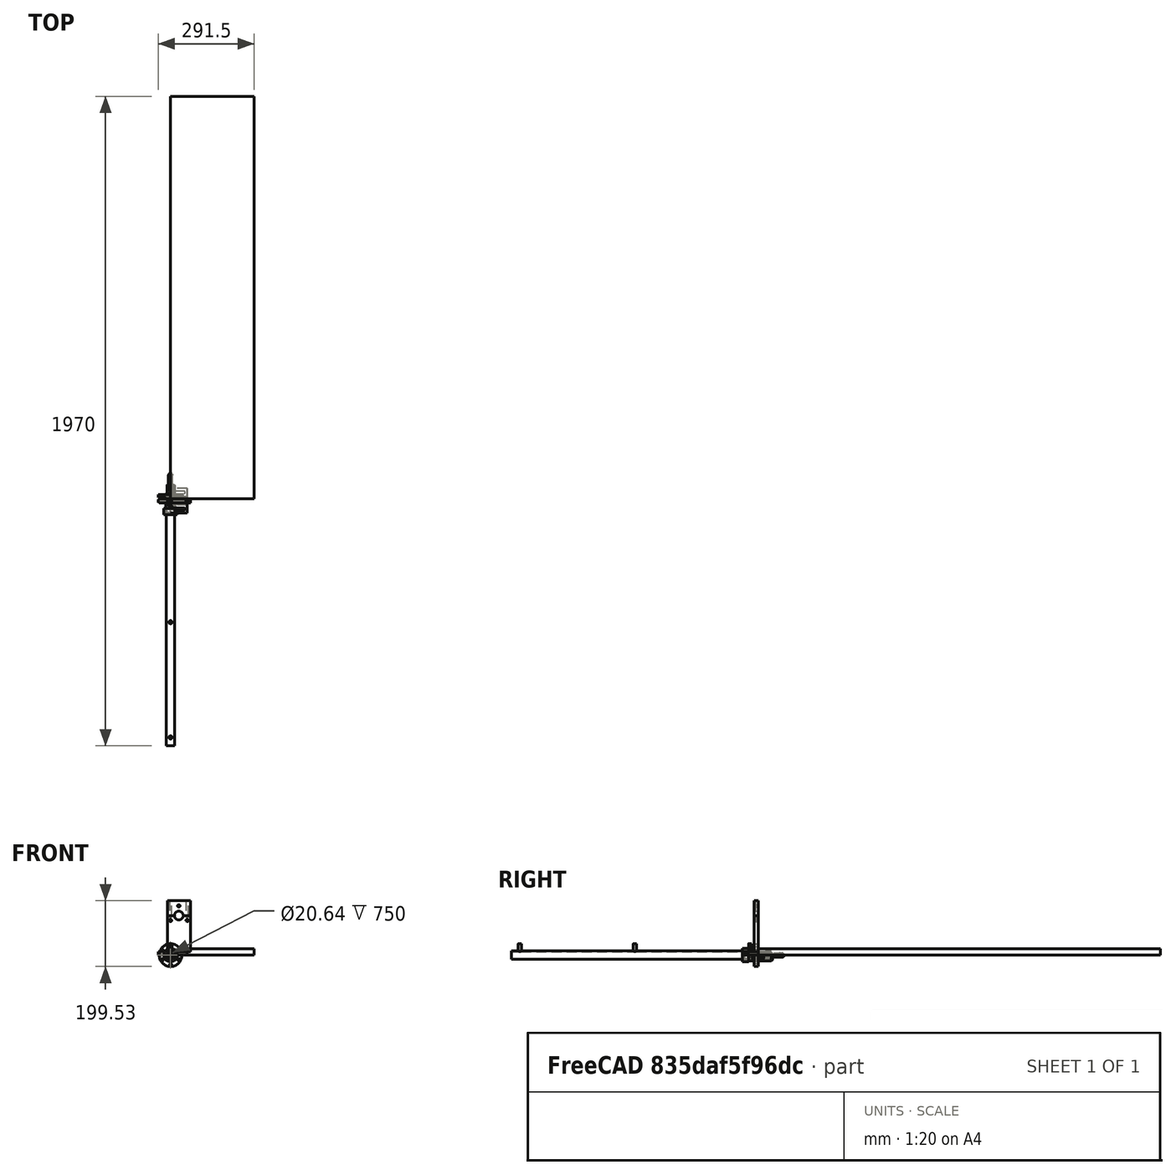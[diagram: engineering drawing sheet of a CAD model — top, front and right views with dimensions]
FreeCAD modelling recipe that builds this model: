
FCSTD DOCUMENT  (FreeCAD 0.19R24291 (Git))
Label: CEAS2
License: All rights reserved
LicenseURL: http://en.wikipedia.org/wiki/All_rights_reserved
objects: Part::Feature×57, Sketcher::SketchObject×41, PartDesign::Pad×41, PartDesign::Body×41, Part::Cut×34, Part::Compound2×12, App::Part×10, TechDraw::DrawViewPart×8, TechDraw::DrawViewDimension×4, TechDraw::DrawViewBalloon×4, TechDraw::DrawViewAnnotation×4, Part::MultiFuse×3, TechDraw::DrawSVGTemplate×1, TechDraw::DrawPage×1
note: 258 computed .brp shape members not serialized (recipe doc carries the construction recipe); baked Part::Feature solids carry a one-line shape summary decoded from their .brp

FEATURE [Sketcher::SketchObject] Sketch
  FullyConstrained = true
  MapMode = 5
  Support = -> [XY_Plane001]
  sketch-geometry (4):
    g0: LineSegment StartX=0 StartY=1220 StartZ=0 EndX=254 EndY=1220 EndZ=0
    g1: LineSegment StartX=254 StartY=1220 StartZ=0 EndX=254 EndY=0 EndZ=0
    g2: LineSegment StartX=254 StartY=0 StartZ=0 EndX=0 EndY=0 EndZ=0
    g3: LineSegment StartX=0 StartY=0 StartZ=0 EndX=0 EndY=1220 EndZ=0
  constraints (11):
    c: Coincident(g0,g1)
    c: Coincident(g1,g2)
    c: Coincident(g2,g3)
    c: Coincident(g3,g0)
    c: Horizontal(g0)
    c: Horizontal(g2)
    c: Vertical(g1)
    c: Vertical(g3)
    c: DistanceY(g3,g3) = 1220
    c: Coincident(g2,g-1)
    c: DistanceX(g2,g2) = 254
FEATURE [PartDesign::Pad] Pad
  AllowMultiFace = false
  Direction = (1,1,1)
  Length = 19.05
  Length2 = 100
  Profile = -> Sketch
  Type = 0
FEATURE [PartDesign::Body] Body  label="BasePlate001"
  Group = -> [Sketch,Pad]
  Origin = -> Origin001
  Tip = -> Pad
FEATURE [App::Part] Part  label="BasePlate"
  Group = -> [Body]
  Origin = -> Origin
FEATURE [Sketcher::SketchObject] Sketch001
  FullyConstrained = true
  MapMode = 5
  Placement = pos=(0,0,0) rot=(1,0,0;1.5708rad)
  Support = -> [XZ_Plane003]
  sketch-geometry (6):
    g0: LineSegment StartX=0 StartY=0 StartZ=0 EndX=0 EndY=110 EndZ=0
    g1: LineSegment StartX=0 StartY=110 StartZ=0 EndX=21.675 EndY=110 EndZ=0
    g2: ArcOfCircle CenterX=35 CenterY=110 CenterZ=0 NormalX=0 NormalY=0 NormalZ=1 AngleXU=0 Radius=13.325 StartAngle=3.14159 EndAngle=6.28319
    g3: LineSegment StartX=48.325 StartY=110 StartZ=0 EndX=70 EndY=110 EndZ=0
    g4: LineSegment StartX=70 StartY=110 StartZ=0 EndX=70 EndY=0 EndZ=0
    g5: LineSegment StartX=70 StartY=0 StartZ=0 EndX=0 EndY=0 EndZ=0
  constraints (18):
    c: DistanceX(g5,g5) = 70
    c: Coincident(g5,g0)
    c: Coincident(g1,g2)
    c: Coincident(g1,g0)
    c: Coincident(g2,g3)
    c: Coincident(g3,g4)
    c: Coincident(g5,g4)
    c: Diameter(g2) = 26.65
    c: Parallel(g0,g4)
    c: DistanceY(g4,g4) = 110
    c: Equal(g0,g4)
    c: Equal(g3,g1)
    c: Perpendicular(g5,g0)
    c: Perpendicular(g4,g3)
    c: Vertical(g0)
    c: Perpendicular(g0,g1)
    c: Coincident(g0,g-1)
    c: DistanceX(g1,g2) = 26.65
FEATURE [Sketcher::SketchObject] Sketch002
  FullyConstrained = true
  MapMode = 5
  Placement = pos=(0,0,0) rot=(1,0,0;1.5708rad)
  Support = -> [XZ_Plane004]
  sketch-geometry (6):
    g0: LineSegment StartX=-20 StartY=110 StartZ=0 EndX=-20 EndY=155 EndZ=0
    g1: LineSegment StartX=-20 StartY=155 StartZ=0 EndX=50 EndY=155 EndZ=0
    g2: LineSegment StartX=50 StartY=155 StartZ=0 EndX=50 EndY=110 EndZ=0
    g3: LineSegment StartX=50 StartY=110 StartZ=0 EndX=28.325 EndY=110 EndZ=0
    g4: LineSegment StartX=-20 StartY=110 StartZ=0 EndX=1.675 EndY=110 EndZ=0
    g5: ArcOfCircle CenterX=15 CenterY=110 CenterZ=0 NormalX=0 NormalY=0 NormalZ=1 AngleXU=0 Radius=13.325 StartAngle=2.48459e-06 EndAngle=3.14159
  constraints (19):
    c: Diameter(g5) = 26.65
    c: DistanceX(g1,g1) = 70
    c: Coincident(g0,g1)
    c: Coincident(g1,g2)
    c: Coincident(g2,g3)
    c: Coincident(g5,g3)
    c: Coincident(g5,g4)
    c: Coincident(g0,g4)
    c: DistanceY(g2,g2) = 45
    c: Equal(g2,g0)
    c: Horizontal(g4)
    c: Equal(g4,g3)
    c: Vertical(g0)
    c: Horizontal(g1)
    c: Perpendicular(g2,g1)
    c: Perpendicular(g2,g3)
    c: DistanceY(g-1,g0) = 110
    c: DistanceX(g-1,g2) = 50
    c: DistanceX(g4,g3) = 26.65
FEATURE [PartDesign::Pad] Pad001
  AllowMultiFace = false
  Direction = (1,1,1)
  Length = 12.7
  Length2 = 100
  Placement = pos=(0,0,0) rot=(1,0,0;1.5708rad)
  Profile = -> Sketch001
  Type = 0
FEATURE [PartDesign::Body] Body001  label="BraceLower"
  Group = -> [Sketch001,Pad001]
  Origin = -> Origin003
  Placement = pos=(-10,0,10) rot=(0,0,1;0rad)
  Tip = -> Pad001
FEATURE [PartDesign::Pad] Pad002
  AllowMultiFace = false
  Direction = (1,1,1)
  Length = 12.7
  Length2 = 100
  Placement = pos=(0,0,0) rot=(1,0,0;1.5708rad)
  Profile = -> Sketch002
  Type = 0
FEATURE [PartDesign::Body] Body002  label="Brace1Upper"
  Group = -> [Sketch002,Pad002]
  Origin = -> Origin004
  Placement = pos=(10,0,10) rot=(0,0,1;0rad)
  Tip = -> Pad002
FEATURE [Part::Feature] Solid  label="19227-E0W"
  Placement = pos=(25,-6.35,5.1905) rot=(1,0,0;1.5708rad)
  shape: bbox 50 x 75 x 10 mm, 234 faces (baked)
FEATURE [Part::Feature] Solid002  label="19225-E0W"
  Placement = pos=(0,0,5) rot=(1,0,0;1.5708rad)
  shape: bbox 75 x 24.99 x 10 mm, 221 faces (baked)
FEATURE [Part::Feature] Solid003
  shape: bbox 25 x 75 x 25 mm, 25 faces (baked)
FEATURE [Part::Feature] Solid004
  shape: bbox 15.88 x 5.969 x 15.88 mm, 19 faces (baked)
FEATURE [Part::Feature] Solid005
  shape: bbox 14.48 x 14.48 x 16.13 mm, 310 faces (baked)
FEATURE [Part::Feature] Solid006
  shape: bbox 2.997 x 2.997 x 3.556 mm, 8 faces (baked)
FEATURE [Part::Feature] Solid007
  shape: bbox 3.52 x 3.049 x 7.519 mm, 25 faces (baked)
FEATURE [Part::Feature] Solid008
  shape: bbox 3.482 x 3.482 x 3.175 mm, 21 faces (baked)
FEATURE [Part::Compound2] Compound  label="23133-E0W"
  Links = -> [Solid003,Solid004,Solid005,Solid006,Solid007,Solid008]
  Placement = pos=(-1.27,-4.75,41.95) rot=(1,0,0;1.5708rad)
FEATURE [Part::Feature] Solid009
  shape: bbox 12.67 x 75.01 x 12.67 mm, 32 faces (baked)
FEATURE [Part::Feature] Solid010
  shape: bbox 4.001 x 12 x 4.001 mm, 40 faces (baked)
FEATURE [Part::Compound2] Compound001  label="0332-E0W"
  Links = -> [Solid009,Solid010]
  Placement = pos=(0,0,22.896) rot=(1,0,0;1.5708rad)
FEATURE [Part::Feature] Solid011
  shape: bbox 30.48 x 37.34 x 10.16 mm, 236 faces (baked)
FEATURE [Part::Feature] Solid012
  shape: bbox 26.29 x 26.29 x 2.032 mm, 29 faces (baked)
FEATURE [Part::Compound2] Compound002  label="0001-E0W"
  Links = -> [Solid011,Solid012]
  Placement = pos=(0,-5.05,120) rot=(1,0,0;1.5708rad)
FEATURE [App::Part] Part003  label="Lens1"
  Group = -> [Solid002,Solid008,Solid006,Solid003,Solid005,Solid007,Solid004,Compound,Solid009,Solid010,Compound001,Solid012,Solid011,Compound002]
  Origin = -> Origin008
  Placement = pos=(127,100,19.05) rot=(0,0,1;0rad)
FEATURE [Part::Feature] Solid013  label="19225-E0W001"
  Placement = pos=(0,0,5) rot=(1,0,0;1.5708rad)
  shape: bbox 75 x 24.99 x 10 mm, 221 faces (baked)
FEATURE [Part::Feature] Solid014
  shape: bbox 25 x 75 x 25 mm, 25 faces (baked)
FEATURE [Part::Feature] Solid015
  shape: bbox 15.88 x 5.969 x 15.88 mm, 19 faces (baked)
FEATURE [Part::Feature] Solid016
  shape: bbox 14.48 x 14.48 x 16.13 mm, 310 faces (baked)
FEATURE [Part::Feature] Solid017
  shape: bbox 2.997 x 2.997 x 3.556 mm, 8 faces (baked)
FEATURE [Part::Feature] Solid018
  shape: bbox 3.52 x 3.049 x 7.519 mm, 25 faces (baked)
FEATURE [Part::Feature] Solid019
  shape: bbox 3.482 x 3.482 x 3.175 mm, 21 faces (baked)
FEATURE [Part::Compound2] Compound003  label="23133-E0W001"
  Links = -> [Solid014,Solid015,Solid016,Solid017,Solid018,Solid019]
  Placement = pos=(-1.27,-4.75,41.95) rot=(1,0,0;1.5708rad)
FEATURE [Part::Feature] Solid020
  shape: bbox 12.67 x 75.01 x 12.67 mm, 32 faces (baked)
FEATURE [Part::Feature] Solid021
  shape: bbox 4.001 x 12 x 4.001 mm, 40 faces (baked)
FEATURE [Part::Compound2] Compound004  label="0332-E0W001"
  Links = -> [Solid020,Solid021]
  Placement = pos=(0,0,22.896) rot=(1,0,0;1.5708rad)
FEATURE [Part::Feature] Solid022
  shape: bbox 30.48 x 37.34 x 10.16 mm, 236 faces (baked)
FEATURE [Part::Feature] Solid023
  shape: bbox 26.29 x 26.29 x 2.032 mm, 29 faces (baked)
FEATURE [Part::Compound2] Compound005  label="0001-E0W001"
  Links = -> [Solid022,Solid023]
  Placement = pos=(0,-5.05,120) rot=(1,0,0;1.5708rad)
FEATURE [App::Part] Part004  label="Lens2"
  Group = -> [Solid013,Solid019,Solid017,Solid014,Solid016,Solid018,Solid015,Compound003,Solid020,Solid021,Compound004,Solid023,Solid022,Compound005]
  Origin = -> Origin009
  Placement = pos=(127,200,19.05) rot=(0,0,1;0rad)
FEATURE [Part::Feature] Solid024
  shape: bbox 26.29 x 26.29 x 2.032 mm, 29 faces (baked)
FEATURE [Part::Feature] Solid025
  shape: bbox 30.48 x 37.34 x 10.16 mm, 236 faces (baked)
FEATURE [Part::Compound2] Compound006  label="0001-E0W002"
  Links = -> [Solid025,Solid024]
  Placement = pos=(0,-5.05,120) rot=(1,0,0;1.5708rad)
FEATURE [Part::Feature] Solid026
  shape: bbox 2.997 x 2.997 x 3.556 mm, 8 faces (baked)
FEATURE [Part::Feature] Solid027
  shape: bbox 14.48 x 14.48 x 16.13 mm, 310 faces (baked)
FEATURE [Part::Feature] Solid028
  shape: bbox 25 x 75 x 25 mm, 25 faces (baked)
FEATURE [Part::Feature] Solid029
  shape: bbox 15.88 x 5.969 x 15.88 mm, 19 faces (baked)
FEATURE [Part::Feature] Solid030
  shape: bbox 3.482 x 3.482 x 3.175 mm, 21 faces (baked)
FEATURE [Part::Feature] Solid031
  shape: bbox 3.52 x 3.049 x 7.519 mm, 25 faces (baked)
FEATURE [Part::Compound2] Compound007  label="23133-E0W002"
  Links = -> [Solid028,Solid029,Solid027,Solid026,Solid031,Solid030]
  Placement = pos=(-1.27,-4.75,41.95) rot=(1,0,0;1.5708rad)
FEATURE [Part::Feature] Solid032  label="19225-E0W002"
  Placement = pos=(0,0,5) rot=(1,0,0;1.5708rad)
  shape: bbox 75 x 24.99 x 10 mm, 221 faces (baked)
FEATURE [Part::Feature] Solid033
  shape: bbox 12.67 x 75.01 x 12.67 mm, 32 faces (baked)
FEATURE [Part::Feature] Solid034
  shape: bbox 4.001 x 12 x 4.001 mm, 40 faces (baked)
FEATURE [Part::Compound2] Compound008  label="0332-E0W002"
  Links = -> [Solid033,Solid034]
  Placement = pos=(0,0,22.896) rot=(1,0,0;1.5708rad)
FEATURE [App::Part] Part005  label="Lens3"
  Group = -> [Solid032,Solid030,Solid026,Solid028,Solid027,Solid031,Solid029,Compound007,Solid033,Solid034,Compound008,Solid024,Solid025,Compound006]
  Origin = -> Origin010
  Placement = pos=(127,1150,19.05) rot=(0,0,1;0rad)
FEATURE [Sketcher::SketchObject] Sketch005
  FullyConstrained = true
  MapMode = 5
  Placement = pos=(0,0,0) rot=(1,0,0;1.5708rad)
  Support = -> [XZ_Plane015]
  sketch-geometry (2):
    g0: Circle CenterX=0 CenterY=0 CenterZ=0 NormalX=0 NormalY=0 NormalZ=1 AngleXU=0 Radius=12.7
    g1: Circle CenterX=0 CenterY=0 CenterZ=0 NormalX=0 NormalY=0 NormalZ=1 AngleXU=0 Radius=10.3187
  constraints (4):
    c: Coincident(g0,g-1)
    c: Coincident(g1,g0)
    c: Diameter(g0) = 25.4
    c: Diameter(g1) = 20.6375
FEATURE [PartDesign::Pad] Pad005
  Direction = (1,1,1)
  Length = 750
  Length2 = 100
  Placement = pos=(0,0,0) rot=(1,0,0;1.5708rad)
  Profile = -> Sketch005
  Type = 0
FEATURE [PartDesign::Body] Body005
  Group = -> [Sketch005,Pad005]
  Origin = -> Origin015
  Tip = -> Pad005
FEATURE [Sketcher::SketchObject] Sketch006
  FullyConstrained = true
  MapMode = 5
  Support = -> [XY_Plane016]
  sketch-geometry (2):
    g0: Circle CenterX=0 CenterY=0 CenterZ=0 NormalX=0 NormalY=0 NormalZ=1 AngleXU=0 Radius=4.7625
    g1: Circle CenterX=0 CenterY=0 CenterZ=0 NormalX=0 NormalY=0 NormalZ=1 AngleXU=0 Radius=3.8695
  constraints (4):
    c: Coincident(g0,g-1)
    c: Coincident(g1,g0)
    c: Diameter(g0) = 9.525
    c: Diameter(g1) = 7.739
FEATURE [PartDesign::Pad] Pad006
  Direction = (1,1,1)
  Length = 25.4
  Length2 = 100
  Profile = -> Sketch006
  Type = 0
FEATURE [PartDesign::Body] Body006
  Group = -> [Sketch006,Pad006]
  Origin = -> Origin016
  Placement = pos=(0,-25.4,9.55) rot=(0,0,1;0rad)
  Tip = -> Pad006
FEATURE [Sketcher::SketchObject] Sketch007
  FullyConstrained = true
  MapMode = 5
  Support = -> [XY_Plane017]
  sketch-geometry (2):
    g0: Circle CenterX=0 CenterY=0 CenterZ=0 NormalX=0 NormalY=0 NormalZ=1 AngleXU=0 Radius=4.7625
    g1: Circle CenterX=0 CenterY=0 CenterZ=0 NormalX=0 NormalY=0 NormalZ=1 AngleXU=0 Radius=3.8695
  constraints (4):
    c: Coincident(g0,g-1)
    c: Coincident(g1,g0)
    c: Diameter(g0) = 9.525
    c: Diameter(g1) = 7.739
FEATURE [PartDesign::Pad] Pad007
  Direction = (1,1,1)
  Length = 25.4
  Length2 = 100
  Profile = -> Sketch007
  Type = 0
FEATURE [PartDesign::Body] Body007
  Group = -> [Sketch007,Pad007]
  Origin = -> Origin017
  Placement = pos=(0,-375,9.55) rot=(0,0,1;0rad)
  Tip = -> Pad007
FEATURE [Sketcher::SketchObject] Sketch008
  FullyConstrained = true
  MapMode = 5
  Support = -> [XY_Plane018]
  sketch-geometry (2):
    g0: Circle CenterX=0 CenterY=0 CenterZ=0 NormalX=0 NormalY=0 NormalZ=1 AngleXU=0 Radius=4.7625
    g1: Circle CenterX=0 CenterY=0 CenterZ=0 NormalX=0 NormalY=0 NormalZ=1 AngleXU=0 Radius=3.8695
  constraints (4):
    c: Coincident(g0,g-1)
    c: Coincident(g1,g0)
    c: Diameter(g0) = 9.525
    c: Diameter(g1) = 7.739
FEATURE [PartDesign::Pad] Pad008
  Direction = (1,1,1)
  Length = 25.4
  Length2 = 100
  Profile = -> Sketch008
  Type = 0
FEATURE [PartDesign::Body] Body008
  Group = -> [Sketch008,Pad008]
  Origin = -> Origin018
  Placement = pos=(0,-724.6,9.55) rot=(0,0,1;0rad)
  Tip = -> Pad008
FEATURE [Sketcher::SketchObject] Sketch009
  FullyConstrained = true
  MapMode = 5
  Support = -> [XY_Plane020]
  sketch-geometry (1):
    g0: Circle CenterX=0 CenterY=0 CenterZ=0 NormalX=0 NormalY=0 NormalZ=1 AngleXU=0 Radius=4.7625
  constraints (2):
    c: Coincident(g0,g-1)
    c: Diameter(g0) = 9.525
FEATURE [PartDesign::Pad] Pad009
  Direction = (1,1,1)
  Length = 25.4
  Length2 = 100
  Profile = -> Sketch009
  Type = 0
FEATURE [PartDesign::Body] Body009
  Group = -> [Sketch009,Pad009]
  Origin = -> Origin019
  Placement = pos=(0,-25.4,0) rot=(0,0,1;0rad)
  Tip = -> Pad009
FEATURE [Sketcher::SketchObject] Sketch010
  FullyConstrained = true
  MapMode = 5
  Support = -> [XY_Plane021]
  sketch-geometry (1):
    g0: Circle CenterX=0 CenterY=0 CenterZ=0 NormalX=0 NormalY=0 NormalZ=1 AngleXU=0 Radius=4.7625
  constraints (2):
    c: Coincident(g0,g-1)
    c: Diameter(g0) = 9.525
FEATURE [PartDesign::Pad] Pad010
  Direction = (1,1,1)
  Length = 25.4
  Length2 = 100
  Profile = -> Sketch010
  Type = 0
FEATURE [PartDesign::Body] Body010
  Group = -> [Sketch010,Pad010]
  Origin = -> Origin020
  Placement = pos=(0,-375,0) rot=(0,0,1;0rad)
  Tip = -> Pad010
FEATURE [Sketcher::SketchObject] Sketch011
  FullyConstrained = true
  MapMode = 5
  Support = -> [XY_Plane022]
  sketch-geometry (1):
    g0: Circle CenterX=0 CenterY=0 CenterZ=0 NormalX=0 NormalY=0 NormalZ=1 AngleXU=0 Radius=4.7625
  constraints (2):
    c: Coincident(g0,g-1)
    c: Diameter(g0) = 9.525
FEATURE [PartDesign::Pad] Pad011
  Direction = (1,1,1)
  Length = 25.4
  Length2 = 100
  Profile = -> Sketch011
  Type = 0
FEATURE [PartDesign::Body] Body011
  Group = -> [Sketch011,Pad011]
  Origin = -> Origin021
  Placement = pos=(0,-724.6,0) rot=(0,0,1;0rad)
  Tip = -> Pad011
FEATURE [Part::Cut] Cut
  Base = -> Body005
  Tool = -> Body009
FEATURE [Part::Cut] Cut001
  Base = -> Cut
  Tool = -> Body010
FEATURE [Part::Cut] Cut002
  Base = -> Cut001
  Tool = -> Body011
FEATURE [Sketcher::SketchObject] Sketch012
  FullyConstrained = true
  MapMode = 5
  Placement = pos=(0,0,0) rot=(1,0,0;1.5708rad)
  Support = -> [XZ_Plane022]
  sketch-geometry (1):
    g0: Circle CenterX=0 CenterY=0 CenterZ=0 NormalX=0 NormalY=0 NormalZ=1 AngleXU=0 Radius=10.3187
  constraints (2):
    c: Coincident(g0,g-1)
    c: Diameter(g0) = 20.6375
FEATURE [PartDesign::Pad] Pad012
  Direction = (1,1,1)
  Length = 750
  Length2 = 100
  Placement = pos=(0,0,0) rot=(1,0,0;1.5708rad)
  Profile = -> Sketch012
  Type = 0
FEATURE [PartDesign::Body] Body012
  Group = -> [Sketch012,Pad012]
  Origin = -> Origin022
  Tip = -> Pad012
FEATURE [Part::Cut] Cut003
  Base = -> Body006
  Tool = -> Body012
FEATURE [Part::Cut] Cut004
  Base = -> Body007
  Tool = -> Body012
FEATURE [Part::Cut] Cut005
  Base = -> Body008
  Tool = -> Body012
FEATURE [Part::MultiFuse] Fusion
  Shapes = -> [Cut002,Cut005,Cut004,Cut003]
FEATURE [App::Part] Part007  label="Cavity"
  Group = -> [Body005,Body006,Body007,Body008,Body009,Body010,Body011,Cut,Cut001,Cut002,Body012,Cut005,Cut004,Cut003,Fusion]
  Origin = -> Origin014
  Placement = pos=(127,310.4,139.05) rot=(0,0,1;3.14159rad)
FEATURE [Sketcher::SketchObject] Sketch013
  FullyConstrained = true
  MapMode = 5
  Placement = pos=(0,0,0) rot=(1,0,0;1.5708rad)
  Support = -> [XZ_Plane024]
  sketch-geometry (2):
    g0: Circle CenterX=0 CenterY=0 CenterZ=0 NormalX=0 NormalY=0 NormalZ=1 AngleXU=0 Radius=34.5281
    g1: Circle CenterX=0 CenterY=0 CenterZ=0 NormalX=0 NormalY=0 NormalZ=1 AngleXU=0 Radius=14.2875
  constraints (4):
    c: Coincident(g0,g-1)
    c: Coincident(g1,g0)
    c: Diameter(g1) = 28.575
    c: Diameter(g0) = 69.0563
FEATURE [PartDesign::Pad] Pad013
  Direction = (1,1,1)
  Length = 12.7
  Length2 = 100
  Placement = pos=(0,0,0) rot=(1,0,0;1.5708rad)
  Profile = -> Sketch013
  Type = 0
FEATURE [PartDesign::Body] Body013
  Group = -> [Sketch013,Pad013]
  Origin = -> Origin024
  Tip = -> Pad013
FEATURE [Sketcher::SketchObject] Sketch014
  FullyConstrained = true
  MapMode = 5
  Placement = pos=(0,0,0) rot=(1,0,0;1.5708rad)
  Support = -> [XZ_Plane025]
  sketch-geometry (1):
    g0: Circle CenterX=0 CenterY=29.3687 CenterZ=0 NormalX=0 NormalY=0 NormalZ=1 AngleXU=0 Radius=3.57187
  constraints (3):
    c: PointOnObject(g0,g-2)
    c: DistanceY(g-1,g0) = 29.3687
    c: Diameter(g0) = 7.14375
FEATURE [PartDesign::Pad] Pad014
  Direction = (1,1,1)
  Length = 13
  Length2 = 100
  Placement = pos=(0,0,0) rot=(1,0,0;1.5708rad)
  Profile = -> Sketch014
  Type = 0
FEATURE [PartDesign::Body] Body014
  Group = -> [Sketch014,Pad014]
  Origin = -> Origin025
  Tip = -> Pad014
FEATURE [Part::Cut] Cut006
  Base = -> Body013
  Placement = pos=(0,0,0) rot=(0,1,0;1.0472rad)
  Tool = -> Body014
FEATURE [Part::Cut] Cut007
  Base = -> Cut006
  Placement = pos=(0,0,0) rot=(0,1,0;1.0472rad)
  Tool = -> Body014
FEATURE [Part::Cut] Cut008
  Base = -> Cut007
  Placement = pos=(0,0,0) rot=(0,1,0;1.0472rad)
  Tool = -> Body014
FEATURE [Part::Cut] Cut009
  Base = -> Cut008
  Placement = pos=(0,0,0) rot=(0,1,0;1.0472rad)
  Tool = -> Body014
FEATURE [Part::Cut] Cut010
  Base = -> Cut009
  Placement = pos=(0,0,0) rot=(0,1,0;1.0472rad)
  Tool = -> Body014
FEATURE [Part::Cut] Cut011
  Base = -> Cut010
  Tool = -> Body014
FEATURE [Sketcher::SketchObject] Sketch015
  FullyConstrained = true
  MapMode = 5
  Placement = pos=(0,0,0) rot=(1,0,0;1.5708rad)
  Support = -> [XZ_Plane026]
  sketch-geometry (2):
    g0: Circle CenterX=0 CenterY=0 CenterZ=0 NormalX=0 NormalY=0 NormalZ=1 AngleXU=0 Radius=12.7
    g1: Circle CenterX=0 CenterY=0 CenterZ=0 NormalX=0 NormalY=0 NormalZ=1 AngleXU=0 Radius=14.2875
  constraints (4):
    c: Coincident(g0,g-1)
    c: Coincident(g1,g0)
    c: Diameter(g0) = 25.4
    c: Diameter(g1) = 28.575
FEATURE [PartDesign::Pad] Pad015
  Direction = (1,1,1)
  Length = 29.21
  Length2 = 100
  Placement = pos=(0,0,0) rot=(1,0,0;1.5708rad)
  Profile = -> Sketch015
  Type = 0
FEATURE [PartDesign::Body] Body015
  Group = -> [Sketch015,Pad015]
  Origin = -> Origin026
  Placement = pos=(0,-0.16,0) rot=(0,0,1;0rad)
  Tip = -> Pad015
FEATURE [Sketcher::SketchObject] Sketch016
  FullyConstrained = true
  MapMode = 5
  Placement = pos=(0,0,0) rot=(1,0,0;1.5708rad)
  Support = -> [XZ_Plane027]
  sketch-geometry (2):
    g0: Circle CenterX=0 CenterY=0 CenterZ=0 NormalX=0 NormalY=0 NormalZ=1 AngleXU=0 Radius=12.7
    g1: Circle CenterX=0 CenterY=0 CenterZ=0 NormalX=0 NormalY=0 NormalZ=1 AngleXU=0 Radius=16.6687
  constraints (4):
    c: Coincident(g0,g-1)
    c: Coincident(g1,g0)
    c: Diameter(g0) = 25.4
    c: Diameter(g1) = 33.3375
FEATURE [PartDesign::Pad] Pad016
  Direction = (1,1,1)
  Length = 12.7
  Length2 = 100
  Placement = pos=(0,0,0) rot=(1,0,0;1.5708rad)
  Profile = -> Sketch016
  Type = 0
FEATURE [PartDesign::Body] Body016
  Group = -> [Sketch016,Pad016]
  Origin = -> Origin027
  Placement = pos=(0,-29.37,0) rot=(0,0,1;0rad)
  Tip = -> Pad016
FEATURE [Part::MultiFuse] Fusion001
  Shapes = -> [Cut011,Body015,Body016]
FEATURE [Sketcher::SketchObject] Sketch017
  FullyConstrained = true
  MapMode = 5
  Placement = pos=(0,0,0) rot=(1,0,0;1.5708rad)
  Support = -> [XZ_Plane028]
  sketch-geometry (2):
    g0: Circle CenterX=0 CenterY=0 CenterZ=0 NormalX=0 NormalY=0 NormalZ=1 AngleXU=0 Radius=12.7
    g1: Circle CenterX=0 CenterY=0 CenterZ=0 NormalX=0 NormalY=0 NormalZ=1 AngleXU=0 Radius=16.6687
  constraints (4):
    c: Coincident(g0,g-1)
    c: Coincident(g1,g0)
    c: Diameter(g0) = 25.4
    c: Diameter(g1) = 33.3375
FEATURE [PartDesign::Pad] Pad017
  Direction = (1,1,1)
  Length = 3.175
  Length2 = 100
  Placement = pos=(0,0,0) rot=(1,0,0;1.5708rad)
  Profile = -> Sketch017
  Type = 0
FEATURE [PartDesign::Body] Body017
  Group = -> [Sketch017,Pad017]
  Origin = -> Origin028
  Placement = pos=(0,-42.07,0) rot=(0,0,1;0rad)
  Tip = -> Pad017
FEATURE [Sketcher::SketchObject] Sketch018
  FullyConstrained = true
  MapMode = 5
  Placement = pos=(0,0,0) rot=(1,0,0;1.5708rad)
  Support = -> [XZ_Plane029]
  sketch-geometry (2):
    g0: Circle CenterX=0 CenterY=0 CenterZ=0 NormalX=0 NormalY=0 NormalZ=1 AngleXU=0 Radius=20.2406
    g1: Circle CenterX=0 CenterY=0 CenterZ=0 NormalX=0 NormalY=0 NormalZ=1 AngleXU=0 Radius=12.7
  constraints (4):
    c: Coincident(g0,g-1)
    c: Coincident(g1,g0)
    c: Diameter(g0) = 40.4813
    c: Diameter(g1) = 25.4
FEATURE [PartDesign::Pad] Pad018
  Direction = (1,1,1)
  Length = 19.05
  Length2 = 100
  Placement = pos=(0,0,0) rot=(1,0,0;1.5708rad)
  Profile = -> Sketch018
  Type = 0
FEATURE [PartDesign::Body] Body018
  Group = -> [Sketch018,Pad018]
  Origin = -> Origin029
  Tip = -> Pad018
FEATURE [Sketcher::SketchObject] Sketch019
  FullyConstrained = true
  MapMode = 5
  Placement = pos=(0,0,0) rot=(1,0,0;1.5708rad)
  Support = -> [XZ_Plane030]
  sketch-geometry (1):
    g0: Circle CenterX=0 CenterY=0 CenterZ=0 NormalX=0 NormalY=0 NormalZ=1 AngleXU=0 Radius=16.6687
  constraints (2):
    c: Coincident(g0,g-1)
    c: Diameter(g0) = 33.3375
FEATURE [PartDesign::Pad] Pad019
  Direction = (1,1,1)
  Length = 15.875
  Length2 = 100
  Placement = pos=(0,0,0) rot=(1,0,0;1.5708rad)
  Profile = -> Sketch019
  Type = 0
FEATURE [PartDesign::Body] Body019
  Group = -> [Sketch019,Pad019]
  Origin = -> Origin030
  Tip = -> Pad019
FEATURE [Part::Cut] Cut012
  Base = -> Body018
  Placement = pos=(0,-29.37,0) rot=(0,0,1;0rad)
  Tool = -> Body019
FEATURE [App::Part] Part008  label="CFQuick1"
  Group = -> [Body014,Cut010,Body013,Cut006,Cut008,Cut009,Cut007,Cut011,Body015,Body016,Fusion001,Body017,Body018,Body019,Cut012]
  Origin = -> Origin023
  Placement = pos=(127,274.6,139.05) rot=(0,0,1;3.14159rad)
FEATURE [Sketcher::SketchObject] Sketch020
  FullyConstrained = true
  MapMode = 5
  Placement = pos=(0,0,0) rot=(1,0,0;1.5708rad)
  Support = -> [XZ_Plane031]
  sketch-geometry (1):
    g0: Circle CenterX=0 CenterY=0 CenterZ=0 NormalX=0 NormalY=0 NormalZ=1 AngleXU=0 Radius=3.57187
  constraints (2):
    c: Coincident(g0,g-1)
    c: Diameter(g0) = 7.14375
FEATURE [PartDesign::Pad] Pad020
  Direction = (1,1,1)
  Length = 30
  Length2 = 100
  Placement = pos=(0,0,0) rot=(1,0,0;1.5708rad)
  Profile = -> Sketch020
  Type = 0
FEATURE [PartDesign::Body] Body020
  Group = -> [Sketch020,Pad020]
  Origin = -> Origin031
  Placement = pos=(25,2,149.369) rot=(0,0,1;0rad)
  Tip = -> Pad020
FEATURE [Part::Cut] Cut013
  Base = -> Body002
  Placement = pos=(100,0,0) rot=(0,0,1;0rad)
  Tool = -> Body020
FEATURE [Sketcher::SketchObject] Sketch021
  FullyConstrained = true
  MapMode = 5
  Support = -> [XY_Plane033]
  sketch-geometry (1):
    g0: Circle CenterX=0 CenterY=0 CenterZ=0 NormalX=0 NormalY=0 NormalZ=1 AngleXU=0 Radius=3.57188
  constraints (2):
    c: Coincident(g0,g-1)
    c: Diameter(g0) = 7.14375
FEATURE [PartDesign::Pad] Pad021
  Direction = (1,1,1)
  Length = 55
  Length2 = 100
  Profile = -> Sketch021
  Type = 0
FEATURE [PartDesign::Body] Body021
  Group = -> [Sketch021,Pad021]
  Origin = -> Origin032
  Placement = pos=(100,-6.35,115) rot=(0,0,1;0rad)
  Tip = -> Pad021
FEATURE [Part::Cut] Cut014
  Base = -> Cut013
  Tool = -> Body021
FEATURE [Sketcher::SketchObject] Sketch022
  FullyConstrained = true
  MapMode = 5
  Support = -> [XY_Plane034]
  sketch-geometry (1):
    g0: Circle CenterX=0 CenterY=0 CenterZ=0 NormalX=0 NormalY=0 NormalZ=1 AngleXU=0 Radius=3.57187
  constraints (2):
    c: Diameter(g0) = 7.14375
    c: Coincident(g0,g-1)
FEATURE [PartDesign::Pad] Pad022
  Direction = (1,1,1)
  Length = 55
  Length2 = 100
  Profile = -> Sketch022
  Type = 0
FEATURE [PartDesign::Body] Body022
  Group = -> [Sketch022,Pad022]
  Origin = -> Origin033
  Placement = pos=(150,-6.35,115) rot=(0,0,1;0rad)
  Tip = -> Pad022
FEATURE [Part::Cut] Cut015  label="BraceUpper"
  Base = -> Cut014
  Placement = pos=(-100,0,0) rot=(0,0,1;0rad)
  Tool = -> Body022
FEATURE [Sketcher::SketchObject] Sketch023
  FullyConstrained = true
  MapMode = 5
  Placement = pos=(0,0,0) rot=(1,0,0;1.5708rad)
  Support = -> [XZ_Plane034]
  sketch-geometry (1):
    g0: Circle CenterX=0 CenterY=0 CenterZ=0 NormalX=0 NormalY=0 NormalZ=1 AngleXU=0 Radius=3.57188
  constraints (2):
    c: Coincident(g0,g-1)
    c: Diameter(g0) = 7.14375
FEATURE [PartDesign::Pad] Pad023
  Direction = (1,1,1)
  Length = 33.7
  Length2 = 100
  Placement = pos=(0,0,0) rot=(1,0,0;1.5708rad)
  Profile = -> Sketch023
  Type = 0
FEATURE [PartDesign::Body] Body023
  Group = -> [Sketch023,Pad023]
  Origin = -> Origin034
  Placement = pos=(-0.434083,5,105.316) rot=(0,0,1;0rad)
  Tip = -> Pad023
FEATURE [Part::Cut] Cut016
  Base = -> Body001
  Tool = -> Body023
FEATURE [Sketcher::SketchObject] Sketch024
  FullyConstrained = true
  MapMode = 5
  Placement = pos=(0,0,0) rot=(1,0,0;1.5708rad)
  Support = -> [XZ_Plane035]
  sketch-geometry (1):
    g0: Circle CenterX=0 CenterY=0 CenterZ=0 NormalX=0 NormalY=0 NormalZ=1 AngleXU=0 Radius=3.57187
  constraints (2):
    c: Coincident(g0,g-1)
    c: Diameter(g0) = 7.14375
FEATURE [PartDesign::Pad] Pad024
  Direction = (1,1,1)
  Length = 50
  Length2 = 100
  Placement = pos=(0,0,0) rot=(1,0,0;1.5708rad)
  Profile = -> Sketch024
  Type = 0
FEATURE [PartDesign::Body] Body024
  Group = -> [Sketch024,Pad024]
  Origin = -> Origin035
  Placement = pos=(50.4341,10,105.316) rot=(0,0,1;0rad)
  Tip = -> Pad024
FEATURE [Part::Cut] Cut017
  Base = -> Cut016
  Placement = pos=(100,0,0) rot=(0,0,1;0rad)
  Tool = -> Body024
FEATURE [Sketcher::SketchObject] Sketch025
  FullyConstrained = true
  MapMode = 5
  Support = -> [XY_Plane037]
  sketch-geometry (1):
    g0: Circle CenterX=0 CenterY=0 CenterZ=0 NormalX=0 NormalY=0 NormalZ=1 AngleXU=0 Radius=3.57187
  constraints (2):
    c: Coincident(g0,g-1)
    c: Diameter(g0) = 7.14375
FEATURE [PartDesign::Pad] Pad025
  Direction = (1,1,1)
  Length = 6
  Length2 = 100
  Profile = -> Sketch025
  Type = 0
FEATURE [PartDesign::Body] Body025
  Group = -> [Sketch025,Pad025]
  Origin = -> Origin036
  Placement = pos=(100,-6.35,115) rot=(0,0,1;0rad)
  Tip = -> Pad025
FEATURE [Sketcher::SketchObject] Sketch026
  FullyConstrained = true
  MapMode = 5
  Support = -> [XY_Plane038]
  sketch-geometry (1):
    g0: Circle CenterX=0 CenterY=0 CenterZ=0 NormalX=0 NormalY=0 NormalZ=1 AngleXU=0 Radius=3.57187
  constraints (2):
    c: Coincident(g0,g-1)
    c: Diameter(g0) = 7.14375
FEATURE [PartDesign::Pad] Pad026
  Direction = (1,1,1)
  Length = 6
  Length2 = 100
  Profile = -> Sketch026
  Type = 0
FEATURE [PartDesign::Body] Body026
  Group = -> [Sketch026,Pad026]
  Origin = -> Origin037
  Placement = pos=(150,-6.35,115) rot=(0,0,1;0rad)
  Tip = -> Pad026
FEATURE [TechDraw::DrawSVGTemplate] Template
  EditableTexts = FC-SC=0.75
  Height = 210
  Orientation = 1
  Width = 297
FEATURE [TechDraw::DrawViewPart] View  label="Frente1"
  CoarseView = false
  Direction = (0,-1,0)
  Focus = 100
  HardHidden = false
  IsoCount = 0
  IsoHidden = false
  IsoVisible = false
  LockPosition = false
  Perspective = false
  Rotation = 0
  Scale = 0.75
  ScaleType = 0
  SeamHidden = false
  SeamVisible = true
  SmoothHidden = false
  SmoothVisible = true
  Source = -> [Cut015]
  X = 56.2727
  XDirection = (1,0,0)
  Y = 165.031
FEATURE [TechDraw::DrawViewPart] View001  label="Arriba1"
  CoarseView = false
  Direction = (0,0,1)
  Focus = 100
  HardHidden = false
  IsoCount = 0
  IsoHidden = false
  IsoVisible = false
  LockPosition = false
  Perspective = false
  Rotation = 0
  Scale = 0.75
  ScaleType = 0
  SeamHidden = false
  SeamVisible = true
  SmoothHidden = false
  SmoothVisible = true
  Source = -> [Cut015]
  X = 56.2419
  XDirection = (-1,0,0)
  Y = 120.161
FEATURE [TechDraw::DrawViewPart] View002  label="Abajo1"
  CoarseView = false
  Direction = (0,0,-1)
  Focus = 100
  HardHidden = false
  IsoCount = 0
  IsoHidden = false
  IsoVisible = false
  LockPosition = false
  Perspective = false
  Rotation = 0
  Scale = 0.75
  ScaleType = 0
  SeamHidden = false
  SeamVisible = true
  SmoothHidden = false
  SmoothVisible = true
  Source = -> [Cut015]
  X = 56.2419
  XDirection = (1,0,0)
  Y = 93.0645
FEATURE [TechDraw::DrawViewPart] View003
  CoarseView = false
  Direction = (-0.577,-0.577,0.577)
  Focus = 100
  HardHidden = false
  IsoCount = 0
  IsoHidden = false
  IsoVisible = false
  LockPosition = false
  Perspective = false
  Rotation = 0
  Scale = 0.75
  ScaleType = 0
  SeamHidden = false
  SeamVisible = true
  SmoothHidden = false
  SmoothVisible = true
  Source = -> [Cut015]
  X = 56.9275
  XDirection = (0.707,-0.707,0)
  Y = 47.3157
FEATURE [TechDraw::DrawViewDimension] Dimension
  Arbitrary = false
  ArbitraryTolerances = false
  EqualTolerance = true
  FormatSpec = %.2f
  FormatSpecOverTolerance = %+.2f
  FormatSpecUnderTolerance = %+.2f
  Inverted = false
  LockPosition = false
  MeasureType = 1
  OverTolerance = 0
  References2D = -> [View]
  Rotation = 0
  Scale = 0.75
  ScaleType = 0
  TheoreticalExact = false
  Type = 2
  UnderTolerance = 0
  X = 35.4376
  Y = 0
FEATURE [TechDraw::DrawViewDimension] Dimension001
  Arbitrary = false
  ArbitraryTolerances = false
  EqualTolerance = true
  FormatSpec = %.2f
  FormatSpecOverTolerance = %+.2f
  FormatSpecUnderTolerance = %+.2f
  Inverted = false
  LockPosition = false
  MeasureType = 1
  OverTolerance = 0
  References2D = -> [View]
  Rotation = 0
  Scale = 0.75
  ScaleType = 0
  TheoreticalExact = false
  Type = 1
  UnderTolerance = 0
  X = 0.353369
  Y = 28.8896
FEATURE [Part::Cut] Cut018
  Base = -> Cut017
  Tool = -> Body025
FEATURE [Part::Cut] Cut019  label="BraceLower001"
  Base = -> Cut018
  Placement = pos=(-100,0,0) rot=(0,0,1;0rad)
  Tool = -> Body026
FEATURE [App::Part] Part001  label="Brace1"
  Group = -> [Body001,Solid,Cut014,Cut013,Body022,Body002,Body021,Body020,Cut015,Body023,Cut016,Body024,Cut017,Body025,Body026,Cut018,Cut019]
  Origin = -> Origin002
  Placement = pos=(102,300,19.05) rot=(0,0,1;0rad)
FEATURE [TechDraw::DrawViewPart] View004  label="Frente2"
  CoarseView = false
  Direction = (0,-1,0)
  Focus = 100
  HardHidden = false
  IsoCount = 0
  IsoHidden = false
  IsoVisible = false
  LockPosition = false
  Perspective = false
  Rotation = 0
  Scale = 0.75
  ScaleType = 0
  SeamHidden = false
  SeamVisible = true
  SmoothHidden = false
  SmoothVisible = true
  Source = -> [Cut019]
  X = 160.161
  XDirection = (1,0,0)
  Y = 152.705
FEATURE [TechDraw::DrawViewPart] View005  label="Arriba2"
  CoarseView = false
  Direction = (0,0,1)
  Focus = 100
  HardHidden = false
  IsoCount = 0
  IsoHidden = false
  IsoVisible = false
  LockPosition = false
  Perspective = false
  Rotation = 0
  Scale = 0.75
  ScaleType = 0
  SeamHidden = false
  SeamVisible = true
  SmoothHidden = false
  SmoothVisible = true
  Source = -> [Cut019]
  X = 159.454
  XDirection = (1,0,0)
  Y = 93.6922
FEATURE [TechDraw::DrawViewPart] View006
  CoarseView = false
  Direction = (-0.577,-0.577,0.577)
  Focus = 100
  HardHidden = false
  IsoCount = 0
  IsoHidden = false
  IsoVisible = false
  LockPosition = false
  Perspective = false
  Rotation = 0
  Scale = 0.75
  ScaleType = 0
  SeamHidden = false
  SeamVisible = true
  SmoothHidden = false
  SmoothVisible = true
  Source = -> [Cut019]
  X = 241.79
  XDirection = (0.707,-0.707,0)
  Y = 141.044
FEATURE [TechDraw::DrawViewPart] View007  label="Abajo2"
  CoarseView = false
  Direction = (0,0,-1)
  Focus = 100
  HardHidden = false
  IsoCount = 0
  IsoHidden = false
  IsoVisible = false
  LockPosition = false
  Perspective = false
  Rotation = 0
  Scale = 0.75
  ScaleType = 0
  SeamHidden = false
  SeamVisible = true
  SmoothHidden = false
  SmoothVisible = true
  Source = -> [Cut019]
  X = 159.454
  XDirection = (1,0,0)
  Y = 71.7833
FEATURE [TechDraw::DrawViewDimension] Dimension002
  Arbitrary = false
  ArbitraryTolerances = false
  EqualTolerance = true
  FormatSpec = %.2f
  FormatSpecOverTolerance = %+.2f
  FormatSpecUnderTolerance = %+.2f
  Inverted = false
  LockPosition = false
  MeasureType = 1
  OverTolerance = 0
  References2D = -> [View004]
  Rotation = 0
  Scale = 0.75
  ScaleType = 0
  TheoreticalExact = false
  Type = 2
  UnderTolerance = 0
  X = 36.4977
  Y = 1.06011
FEATURE [TechDraw::DrawViewDimension] Dimension003
  Arbitrary = false
  ArbitraryTolerances = false
  EqualTolerance = true
  FormatSpec = %.2f
  FormatSpecOverTolerance = %+.2f
  FormatSpecUnderTolerance = %+.2f
  Inverted = false
  LockPosition = false
  MeasureType = 1
  OverTolerance = 0
  References2D = -> [View004]
  Rotation = 0
  Scale = 0.75
  ScaleType = 0
  TheoreticalExact = false
  Type = 1
  UnderTolerance = 0
  X = -4.94717
  Y = -28.5287
FEATURE [TechDraw::DrawViewBalloon] Balloon
  BubbleShape = 0
  EndType = 0
  EndTypeScale = 1
  KinkLength = 5
  LockPosition = false
  OriginX = 1.38961
  OriginY = 40.8445
  Rotation = 0
  Scale = 0.75
  ScaleType = 0
  ShapeScale = 1
  SourceView = -> View004
  Text = 1 1/8"
  TextWrapLen = -1
  X = 6.38295
  Y = 5.78933
FEATURE [TechDraw::DrawViewBalloon] Balloon001
  BubbleShape = 0
  EndType = 0
  EndTypeScale = 1
  KinkLength = 5
  LockPosition = false
  OriginX = 2.32908
  OriginY = 6.97707
  Rotation = 0
  Scale = 0.75
  ScaleType = 0
  ShapeScale = 1
  SourceView = -> View
  Text = 1/4"
  TextWrapLen = -1
  X = 23.3418
  Y = -8.7606
FEATURE [TechDraw::DrawViewBalloon] Balloon002
  BubbleShape = 6
  EndType = 0
  EndTypeScale = 1
  KinkLength = 5
  LockPosition = false
  OriginX = 26.8322
  OriginY = -1.08865
  Rotation = 0
  Scale = 0.75
  ScaleType = 0
  ShapeScale = 1
  SourceView = -> View005
  Text = Tornillos 5mm
  TextWrapLen = -1
  X = 67.2974
  Y = -9.26221
FEATURE [TechDraw::DrawViewBalloon] Balloon003
  BubbleShape = 6
  EndType = 0
  EndTypeScale = 1
  KinkLength = 5
  LockPosition = false
  OriginX = 33.3037
  OriginY = -3.42201
  Rotation = 0
  Scale = 0.75
  ScaleType = 0
  ShapeScale = 1
  SourceView = -> View007
  Text = Tornillos de Base
  TextWrapLen = -1
  X = 79.0672
  Y = -3.59405
FEATURE [TechDraw::DrawViewAnnotation] Annotation
  Font = osifont
  LineSpace = 80
  LockPosition = false
  MaxWidth = -1
  Rotation = 0
  Scale = 0.75
  ScaleType = 0
  Text = Arriba
  TextSize = 5
  TextStyle = 0
  X = 19.9839
  Y = 117
FEATURE [TechDraw::DrawViewAnnotation] Annotation001
  Font = osifont
  LineSpace = 80
  LockPosition = false
  MaxWidth = -1
  Rotation = 0
  Scale = 0.75
  ScaleType = 0
  Text = Abajo
  TextSize = 5
  TextStyle = 0
  X = 18.4355
  Y = 90.2903
FEATURE [TechDraw::DrawViewAnnotation] Annotation002
  Font = osifont
  LineSpace = 80
  LockPosition = false
  MaxWidth = -1
  Rotation = 0
  Scale = 0.75
  ScaleType = 0
  Text = Arriba
  TextSize = 5
  TextStyle = 0
  X = 114.823
  Y = 91.0645
FEATURE [TechDraw::DrawViewAnnotation] Annotation003
  Font = osifont
  LineSpace = 80
  LockPosition = false
  MaxWidth = -1
  Rotation = 0
  Scale = 0.75
  ScaleType = 0
  Text = Abajo
  TextSize = 5
  TextStyle = 0
  X = 114.823
  Y = 69.3871
FEATURE [TechDraw::DrawPage] Page
  KeepUpdated = true
  NextBalloonIndex = 7
  ProjectionType = 0
  Scale = 0.75
  Template = -> Template
  Views = -> [View,View001,View002,View003,Dimension,Dimension001,View004,View005,View006,View007,Dimension002,Dimension003,Balloon,Balloon001,Balloon002,Balloon003,Annotation,Annotation001,Annotation002,Annotation003]
FEATURE [Sketcher::SketchObject] Sketch027
  FullyConstrained = true
  MapMode = 5
  Placement = pos=(0,0,0) rot=(1,0,0;1.5708rad)
  Support = -> [XZ_Plane039]
  sketch-geometry (1):
    g0: Circle CenterX=0 CenterY=0 CenterZ=0 NormalX=0 NormalY=0 NormalZ=1 AngleXU=0 Radius=3.57187
  constraints (2):
    c: Coincident(g0,g-1)
    c: Diameter(g0) = 7.14375
FEATURE [PartDesign::Pad] Pad028
  Direction = (1,1,1)
  Length = 30
  Length2 = 100
  Placement = pos=(0,0,0) rot=(1,0,0;1.5708rad)
  Profile = -> Sketch027
  Type = 0
FEATURE [PartDesign::Body] Body035
  Group = -> [Sketch027,Pad028]
  Origin = -> Origin038
  Placement = pos=(25,2,149.369) rot=(0,0,1;0rad)
  Tip = -> Pad028
FEATURE [Sketcher::SketchObject] Sketch028
  FullyConstrained = true
  MapMode = 5
  Support = -> [XY_Plane040]
  sketch-geometry (1):
    g0: Circle CenterX=0 CenterY=0 CenterZ=0 NormalX=0 NormalY=0 NormalZ=1 AngleXU=0 Radius=3.57188
  constraints (2):
    c: Coincident(g0,g-1)
    c: Diameter(g0) = 7.14375
FEATURE [PartDesign::Pad] Pad027
  Direction = (1,1,1)
  Length = 55
  Length2 = 100
  Profile = -> Sketch028
  Type = 0
FEATURE [PartDesign::Body] Body034
  Group = -> [Sketch028,Pad027]
  Origin = -> Origin039
  Placement = pos=(100,-6.35,115) rot=(0,0,1;0rad)
  Tip = -> Pad027
FEATURE [Sketcher::SketchObject] Sketch029
  FullyConstrained = true
  MapMode = 5
  Support = -> [XY_Plane041]
  sketch-geometry (1):
    g0: Circle CenterX=0 CenterY=0 CenterZ=0 NormalX=0 NormalY=0 NormalZ=1 AngleXU=0 Radius=3.57187
  constraints (2):
    c: Diameter(g0) = 7.14375
    c: Coincident(g0,g-1)
FEATURE [Sketcher::SketchObject] Sketch030
  FullyConstrained = true
  MapMode = 5
  Placement = pos=(0,0,0) rot=(1,0,0;1.5708rad)
  Support = -> [XZ_Plane046]
  sketch-geometry (1):
    g0: Circle CenterX=0 CenterY=0 CenterZ=0 NormalX=0 NormalY=0 NormalZ=1 AngleXU=0 Radius=3.57188
  constraints (2):
    c: Coincident(g0,g-1)
    c: Diameter(g0) = 7.14375
FEATURE [PartDesign::Pad] Pad030
  Direction = (1,1,1)
  Length = 33.7
  Length2 = 100
  Placement = pos=(0,0,0) rot=(1,0,0;1.5708rad)
  Profile = -> Sketch030
  Type = 0
FEATURE [PartDesign::Body] Body027
  Group = -> [Sketch030,Pad030]
  Origin = -> Origin045
  Placement = pos=(-0.434083,5,105.316) rot=(0,0,1;0rad)
  Tip = -> Pad030
FEATURE [Sketcher::SketchObject] Sketch031
  FullyConstrained = true
  MapMode = 5
  Placement = pos=(0,0,0) rot=(1,0,0;1.5708rad)
  Support = -> [XZ_Plane045]
  sketch-geometry (6):
    g0: LineSegment StartX=-20 StartY=110 StartZ=0 EndX=-20 EndY=155 EndZ=0
    g1: LineSegment StartX=-20 StartY=155 StartZ=0 EndX=50 EndY=155 EndZ=0
    g2: LineSegment StartX=50 StartY=155 StartZ=0 EndX=50 EndY=110 EndZ=0
    g3: LineSegment StartX=50 StartY=110 StartZ=0 EndX=28.325 EndY=110 EndZ=0
    g4: LineSegment StartX=-20 StartY=110 StartZ=0 EndX=1.675 EndY=110 EndZ=0
    g5: ArcOfCircle CenterX=15 CenterY=110 CenterZ=0 NormalX=0 NormalY=0 NormalZ=1 AngleXU=0 Radius=13.325 StartAngle=2.48459e-06 EndAngle=3.14159
  constraints (19):
    c: Diameter(g5) = 26.65
    c: DistanceX(g1,g1) = 70
    c: Coincident(g0,g1)
    c: Coincident(g1,g2)
    c: Coincident(g2,g3)
    c: Coincident(g5,g3)
    c: Coincident(g5,g4)
    c: Coincident(g0,g4)
    c: DistanceY(g2,g2) = 45
    c: Equal(g2,g0)
    c: Horizontal(g4)
    c: Equal(g4,g3)
    c: Vertical(g0)
    c: Horizontal(g1)
    c: Perpendicular(g2,g1)
    c: Perpendicular(g2,g3)
    c: DistanceY(g-1,g0) = 110
    c: DistanceX(g-1,g2) = 50
    c: DistanceX(g4,g3) = 26.65
FEATURE [PartDesign::Pad] Pad033
  AllowMultiFace = false
  Direction = (1,1,1)
  Length = 12.7
  Length2 = 100
  Placement = pos=(0,0,0) rot=(1,0,0;1.5708rad)
  Profile = -> Sketch031
  Type = 0
FEATURE [PartDesign::Body] Body033  label="Brace1Upper001"
  Group = -> [Sketch031,Pad033]
  Origin = -> Origin042
  Placement = pos=(10,0,10) rot=(0,0,1;0rad)
  Tip = -> Pad033
FEATURE [Part::Cut] Cut021
  Base = -> Body033
  Placement = pos=(100,0,0) rot=(0,0,1;0rad)
  Tool = -> Body035
FEATURE [Part::Cut] Cut020
  Base = -> Cut021
  Tool = -> Body034
FEATURE [Sketcher::SketchObject] Sketch032
  FullyConstrained = true
  MapMode = 5
  Placement = pos=(0,0,0) rot=(1,0,0;1.5708rad)
  Support = -> [XZ_Plane044]
  sketch-geometry (6):
    g0: LineSegment StartX=0 StartY=0 StartZ=0 EndX=0 EndY=110 EndZ=0
    g1: LineSegment StartX=0 StartY=110 StartZ=0 EndX=21.675 EndY=110 EndZ=0
    g2: ArcOfCircle CenterX=35 CenterY=110 CenterZ=0 NormalX=0 NormalY=0 NormalZ=1 AngleXU=0 Radius=13.325 StartAngle=3.14159 EndAngle=6.28319
    g3: LineSegment StartX=48.325 StartY=110 StartZ=0 EndX=70 EndY=110 EndZ=0
    g4: LineSegment StartX=70 StartY=110 StartZ=0 EndX=70 EndY=0 EndZ=0
    g5: LineSegment StartX=70 StartY=0 StartZ=0 EndX=0 EndY=0 EndZ=0
  constraints (18):
    c: DistanceX(g5,g5) = 70
    c: Coincident(g5,g0)
    c: Coincident(g1,g2)
    c: Coincident(g1,g0)
    c: Coincident(g2,g3)
    c: Coincident(g3,g4)
    c: Coincident(g5,g4)
    c: Diameter(g2) = 26.65
    c: Parallel(g0,g4)
    c: DistanceY(g4,g4) = 110
    c: Equal(g0,g4)
    c: Equal(g3,g1)
    c: Perpendicular(g5,g0)
    c: Perpendicular(g4,g3)
    c: Vertical(g0)
    c: Perpendicular(g0,g1)
    c: Coincident(g0,g-1)
    c: DistanceX(g1,g2) = 26.65
FEATURE [PartDesign::Pad] Pad034
  AllowMultiFace = false
  Direction = (1,1,1)
  Length = 12.7
  Length2 = 100
  Placement = pos=(0,0,0) rot=(1,0,0;1.5708rad)
  Profile = -> Sketch032
  Type = 0
FEATURE [PartDesign::Body] Body032  label="BraceLower002"
  Group = -> [Sketch032,Pad034]
  Origin = -> Origin041
  Placement = pos=(-10,0,10) rot=(0,0,1;0rad)
  Tip = -> Pad034
FEATURE [Sketcher::SketchObject] Sketch033
  FullyConstrained = true
  MapMode = 5
  Placement = pos=(0,0,0) rot=(1,0,0;1.5708rad)
  Support = -> [XZ_Plane047]
  sketch-geometry (1):
    g0: Circle CenterX=0 CenterY=0 CenterZ=0 NormalX=0 NormalY=0 NormalZ=1 AngleXU=0 Radius=3.57187
  constraints (2):
    c: Coincident(g0,g-1)
    c: Diameter(g0) = 7.14375
FEATURE [PartDesign::Pad] Pad032
  Direction = (1,1,1)
  Length = 50
  Length2 = 100
  Placement = pos=(0,0,0) rot=(1,0,0;1.5708rad)
  Profile = -> Sketch033
  Type = 0
FEATURE [PartDesign::Body] Body028
  Group = -> [Sketch033,Pad032]
  Origin = -> Origin046
  Placement = pos=(50.4341,10,105.316) rot=(0,0,1;0rad)
  Tip = -> Pad032
FEATURE [Part::Cut] Cut022
  Base = -> Body032
  Tool = -> Body027
FEATURE [Part::Cut] Cut025
  Base = -> Cut022
  Placement = pos=(100,0,0) rot=(0,0,1;0rad)
  Tool = -> Body028
FEATURE [PartDesign::Pad] Pad035
  Direction = (1,1,1)
  Length = 55
  Length2 = 100
  Profile = -> Sketch029
  Type = 0
FEATURE [PartDesign::Body] Body029
  Group = -> [Sketch029,Pad035]
  Origin = -> Origin043
  Placement = pos=(150,-6.35,115) rot=(0,0,1;0rad)
  Tip = -> Pad035
FEATURE [Part::Cut] Cut024  label="BraceUpper001"
  Base = -> Cut020
  Placement = pos=(-100,0,0) rot=(0,0,1;0rad)
  Tool = -> Body029
FEATURE [Part::Feature] Solid035  label="19227-E0W001"
  Placement = pos=(25,-6.35,5.1905) rot=(1,0,0;1.5708rad)
  shape: bbox 50 x 75 x 10 mm, 234 faces (baked)
FEATURE [Sketcher::SketchObject] Sketch034
  FullyConstrained = true
  MapMode = 5
  Support = -> [XY_Plane042]
  sketch-geometry (1):
    g0: Circle CenterX=0 CenterY=0 CenterZ=0 NormalX=0 NormalY=0 NormalZ=1 AngleXU=0 Radius=3.57187
  constraints (2):
    c: Coincident(g0,g-1)
    c: Diameter(g0) = 7.14375
FEATURE [PartDesign::Pad] Pad029
  Direction = (1,1,1)
  Length = 6
  Length2 = 100
  Profile = -> Sketch034
  Type = 0
FEATURE [PartDesign::Body] Body030
  Group = -> [Sketch034,Pad029]
  Origin = -> Origin047
  Placement = pos=(100,-6.35,115) rot=(0,0,1;0rad)
  Tip = -> Pad029
FEATURE [Part::Cut] Cut026
  Base = -> Cut025
  Tool = -> Body030
FEATURE [Sketcher::SketchObject] Sketch035
  FullyConstrained = true
  MapMode = 5
  Support = -> [XY_Plane043]
  sketch-geometry (1):
    g0: Circle CenterX=0 CenterY=0 CenterZ=0 NormalX=0 NormalY=0 NormalZ=1 AngleXU=0 Radius=3.57187
  constraints (2):
    c: Coincident(g0,g-1)
    c: Diameter(g0) = 7.14375
FEATURE [PartDesign::Pad] Pad031
  Direction = (1,1,1)
  Length = 6
  Length2 = 100
  Profile = -> Sketch035
  Type = 0
FEATURE [PartDesign::Body] Body031
  Group = -> [Sketch035,Pad031]
  Origin = -> Origin044
  Placement = pos=(150,-6.35,115) rot=(0,0,1;0rad)
  Tip = -> Pad031
FEATURE [Part::Cut] Cut023  label="BraceLower003"
  Base = -> Cut026
  Placement = pos=(-100,0,0) rot=(0,0,1;0rad)
  Tool = -> Body031
FEATURE [App::Part] Part009  label="Brace2"
  Group = -> [Body032,Solid035,Cut020,Cut021,Body029,Body033,Body034,Body035,Cut024,Body027,Cut022,Body028,Cut025,Body030,Body031,Cut026,Cut023]
  Origin = -> Origin040
  Placement = pos=(102,1083.74,19.05) rot=(0,0,1;0rad)
FEATURE [Sketcher::SketchObject] Sketch036
  FullyConstrained = true
  MapMode = 5
  Placement = pos=(0,0,0) rot=(1,0,0;1.5708rad)
  Support = -> [XZ_Plane055]
  sketch-geometry (2):
    g0: Circle CenterX=0 CenterY=0 CenterZ=0 NormalX=0 NormalY=0 NormalZ=1 AngleXU=0 Radius=20.2406
    g1: Circle CenterX=0 CenterY=0 CenterZ=0 NormalX=0 NormalY=0 NormalZ=1 AngleXU=0 Radius=12.7
  constraints (4):
    c: Coincident(g0,g-1)
    c: Coincident(g1,g0)
    c: Diameter(g0) = 40.4813
    c: Diameter(g1) = 25.4
FEATURE [Sketcher::SketchObject] Sketch037
  FullyConstrained = true
  MapMode = 5
  Placement = pos=(0,0,0) rot=(1,0,0;1.5708rad)
  Support = -> [XZ_Plane052]
  sketch-geometry (2):
    g0: Circle CenterX=0 CenterY=0 CenterZ=0 NormalX=0 NormalY=0 NormalZ=1 AngleXU=0 Radius=12.7
    g1: Circle CenterX=0 CenterY=0 CenterZ=0 NormalX=0 NormalY=0 NormalZ=1 AngleXU=0 Radius=16.6687
  constraints (4):
    c: Coincident(g0,g-1)
    c: Coincident(g1,g0)
    c: Diameter(g0) = 25.4
    c: Diameter(g1) = 33.3375
FEATURE [Sketcher::SketchObject] Sketch038
  FullyConstrained = true
  MapMode = 5
  Placement = pos=(0,0,0) rot=(1,0,0;1.5708rad)
  Support = -> [XZ_Plane053]
  sketch-geometry (2):
    g0: Circle CenterX=0 CenterY=0 CenterZ=0 NormalX=0 NormalY=0 NormalZ=1 AngleXU=0 Radius=12.7
    g1: Circle CenterX=0 CenterY=0 CenterZ=0 NormalX=0 NormalY=0 NormalZ=1 AngleXU=0 Radius=16.6687
  constraints (4):
    c: Coincident(g0,g-1)
    c: Coincident(g1,g0)
    c: Diameter(g0) = 25.4
    c: Diameter(g1) = 33.3375
FEATURE [PartDesign::Pad] Pad039
  Direction = (1,1,1)
  Length = 3.175
  Length2 = 100
  Placement = pos=(0,0,0) rot=(1,0,0;1.5708rad)
  Profile = -> Sketch038
  Type = 0
FEATURE [PartDesign::Pad] Pad041
  Direction = (1,1,1)
  Length = 12.7
  Length2 = 100
  Placement = pos=(0,0,0) rot=(1,0,0;1.5708rad)
  Profile = -> Sketch037
  Type = 0
FEATURE [PartDesign::Pad] Pad042
  Direction = (1,1,1)
  Length = 19.05
  Length2 = 100
  Placement = pos=(0,0,0) rot=(1,0,0;1.5708rad)
  Profile = -> Sketch036
  Type = 0
FEATURE [Sketcher::SketchObject] Sketch039
  FullyConstrained = true
  MapMode = 5
  Placement = pos=(0,0,0) rot=(1,0,0;1.5708rad)
  Support = -> [XZ_Plane051]
  sketch-geometry (2):
    g0: Circle CenterX=0 CenterY=0 CenterZ=0 NormalX=0 NormalY=0 NormalZ=1 AngleXU=0 Radius=12.7
    g1: Circle CenterX=0 CenterY=0 CenterZ=0 NormalX=0 NormalY=0 NormalZ=1 AngleXU=0 Radius=14.2875
  constraints (4):
    c: Coincident(g0,g-1)
    c: Coincident(g1,g0)
    c: Diameter(g0) = 25.4
    c: Diameter(g1) = 28.575
FEATURE [PartDesign::Pad] Pad036
  Direction = (1,1,1)
  Length = 29.21
  Length2 = 100
  Placement = pos=(0,0,0) rot=(1,0,0;1.5708rad)
  Profile = -> Sketch039
  Type = 0
FEATURE [Sketcher::SketchObject] Sketch040
  FullyConstrained = true
  MapMode = 5
  Placement = pos=(0,0,0) rot=(1,0,0;1.5708rad)
  Support = -> [XZ_Plane049]
  sketch-geometry (2):
    g0: Circle CenterX=0 CenterY=0 CenterZ=0 NormalX=0 NormalY=0 NormalZ=1 AngleXU=0 Radius=34.5281
    g1: Circle CenterX=0 CenterY=0 CenterZ=0 NormalX=0 NormalY=0 NormalZ=1 AngleXU=0 Radius=14.2875
  constraints (4):
    c: Coincident(g0,g-1)
    c: Coincident(g1,g0)
    c: Diameter(g1) = 28.575
    c: Diameter(g0) = 69.0563
FEATURE [PartDesign::Pad] Pad037
  Direction = (1,1,1)
  Length = 12.7
  Length2 = 100
  Placement = pos=(0,0,0) rot=(1,0,0;1.5708rad)
  Profile = -> Sketch040
  Type = 0
FEATURE [Sketcher::SketchObject] Sketch041
  FullyConstrained = true
  MapMode = 5
  Placement = pos=(0,0,0) rot=(1,0,0;1.5708rad)
  Support = -> [XZ_Plane050]
  sketch-geometry (1):
    g0: Circle CenterX=0 CenterY=29.3687 CenterZ=0 NormalX=0 NormalY=0 NormalZ=1 AngleXU=0 Radius=3.57187
  constraints (3):
    c: PointOnObject(g0,g-2)
    c: DistanceY(g-1,g0) = 29.3687
    c: Diameter(g0) = 7.14375
FEATURE [PartDesign::Pad] Pad038
  Direction = (1,1,1)
  Length = 13
  Length2 = 100
  Placement = pos=(0,0,0) rot=(1,0,0;1.5708rad)
  Profile = -> Sketch041
  Type = 0
FEATURE [PartDesign::Body] Body036
  Group = -> [Sketch039,Pad036]
  Origin = -> Origin054
  Placement = pos=(0,-0.16,0) rot=(0,0,1;0rad)
  Tip = -> Pad036
FEATURE [PartDesign::Body] Body037
  Group = -> [Sketch037,Pad041]
  Origin = -> Origin055
  Placement = pos=(0,-29.37,0) rot=(0,0,1;0rad)
  Tip = -> Pad041
FEATURE [PartDesign::Body] Body038
  Group = -> [Sketch036,Pad042]
  Origin = -> Origin050
  Tip = -> Pad042
FEATURE [PartDesign::Body] Body039
  Group = -> [Sketch040,Pad037]
  Origin = -> Origin052
  Tip = -> Pad037
FEATURE [PartDesign::Body] Body040
  Group = -> [Sketch041,Pad038]
  Origin = -> Origin053
  Tip = -> Pad038
FEATURE [Part::Cut] Cut028
  Base = -> Body039
  Placement = pos=(0,0,0) rot=(0,1,0;1.0472rad)
  Tool = -> Body040
FEATURE [Part::Cut] Cut027
  Base = -> Cut028
  Placement = pos=(0,0,0) rot=(0,1,0;1.0472rad)
  Tool = -> Body040
FEATURE [Part::Cut] Cut031
  Base = -> Cut027
  Placement = pos=(0,0,0) rot=(0,1,0;1.0472rad)
  Tool = -> Body040
FEATURE [Part::Cut] Cut032
  Base = -> Cut031
  Placement = pos=(0,0,0) rot=(0,1,0;1.0472rad)
  Tool = -> Body040
FEATURE [Part::Cut] Cut029
  Base = -> Cut032
  Placement = pos=(0,0,0) rot=(0,1,0;1.0472rad)
  Tool = -> Body040
FEATURE [Part::Cut] Cut030
  Base = -> Cut029
  Tool = -> Body040
FEATURE [Part::MultiFuse] Fusion002
  Shapes = -> [Cut030,Body036,Body037]
FEATURE [PartDesign::Body] Body041
  Group = -> [Sketch038,Pad039]
  Origin = -> Origin049
  Placement = pos=(0,-42.07,0) rot=(0,0,1;0rad)
  Tip = -> Pad039
FEATURE [Sketcher::SketchObject] Sketch042
  FullyConstrained = true
  MapMode = 5
  Placement = pos=(0,0,0) rot=(1,0,0;1.5708rad)
  Support = -> [XZ_Plane054]
  sketch-geometry (1):
    g0: Circle CenterX=0 CenterY=0 CenterZ=0 NormalX=0 NormalY=0 NormalZ=1 AngleXU=0 Radius=16.6687
  constraints (2):
    c: Coincident(g0,g-1)
    c: Diameter(g0) = 33.3375
FEATURE [PartDesign::Pad] Pad040
  Direction = (1,1,1)
  Length = 15.875
  Length2 = 100
  Placement = pos=(0,0,0) rot=(1,0,0;1.5708rad)
  Profile = -> Sketch042
  Type = 0
FEATURE [PartDesign::Body] Body042
  Group = -> [Sketch042,Pad040]
  Origin = -> Origin048
  Tip = -> Pad040
FEATURE [Part::Cut] Cut033
  Base = -> Body038
  Placement = pos=(0,-29.37,0) rot=(0,0,1;0rad)
  Tool = -> Body042
FEATURE [App::Part] Part010  label="CFQuick2"
  Group = -> [Body040,Cut029,Body039,Cut028,Cut031,Cut032,Cut027,Cut030,Body036,Body037,Fusion002,Body041,Body038,Body042,Cut033]
  Origin = -> Origin051
  Placement = pos=(127,1096.44,139.05) rot=(0,0,1;0rad)
FEATURE [Part::Feature] Solid038
  shape: bbox 25 x 75 x 25 mm, 25 faces (baked)
FEATURE [Part::Feature] Solid039  label="19225-E0W003"
  Placement = pos=(0,0,5) rot=(1,0,0;1.5708rad)
  shape: bbox 75 x 24.99 x 10 mm, 221 faces (baked)
FEATURE [Part::Feature] Solid040
  shape: bbox 2.997 x 2.997 x 3.556 mm, 8 faces (baked)
FEATURE [Part::Feature] Solid041
  shape: bbox 15.88 x 5.969 x 15.88 mm, 19 faces (baked)
FEATURE [Part::Feature] Solid042
  shape: bbox 14.48 x 14.48 x 16.13 mm, 310 faces (baked)
FEATURE [Part::Feature] Solid043
  shape: bbox 12.67 x 75.01 x 12.67 mm, 32 faces (baked)
FEATURE [Part::Feature] Solid044
  shape: bbox 4.001 x 12 x 4.001 mm, 40 faces (baked)
FEATURE [Part::Compound2] Compound010  label="0332-E0W003"
  Links = -> [Solid043,Solid044]
  Placement = pos=(0,0,18.9) rot=(1,0,0;1.5708rad)
FEATURE [Part::Feature] Solid045
  shape: bbox 3.482 x 3.482 x 3.175 mm, 21 faces (baked)
FEATURE [Part::Feature] Solid046
  shape: bbox 3.52 x 3.049 x 7.519 mm, 25 faces (baked)
FEATURE [Part::Compound2] Compound011  label="23133-E0W003"
  Links = -> [Solid038,Solid041,Solid042,Solid040,Solid046,Solid045]
  Placement = pos=(-1.27,-4.75,41.95) rot=(1,0,0;1.5708rad)
FEATURE [Part::Feature] Solid047
  shape: bbox 42.16 x 42.16 x 12.19 mm, 57 faces (baked)
FEATURE [Part::Feature] Solid048
  shape: bbox 40.64 x 40.64 x 3.304 mm, 146 faces (baked)
FEATURE [Part::Feature] Solid049
  shape: bbox 10.67 x 8.128 x 10.67 mm, 27 faces (baked)
FEATURE [Part::Feature] Solid050
  shape: bbox 8.891 x 7.113 x 7.113 mm, 34 faces (baked)
FEATURE [Part::Feature] Solid051
  shape: bbox 7.113 x 8.891 x 7.113 mm, 34 faces (baked)
FEATURE [Part::Feature] Solid052
  shape: bbox 12.97 x 12.92 x 4.572 mm, 6 faces (baked)
FEATURE [Part::Feature] Solid053
  shape: bbox 33.02 x 33.02 x 11.43 mm, 22 faces (baked)
FEATURE [Part::Feature] Solid054
  shape: bbox 35 x 35 x 3.429 mm, 18 faces (baked)
FEATURE [Part::Feature] Solid055
  shape: bbox 7.332 x 5.588 x 6.35 mm, 28 faces (baked)
FEATURE [Part::Feature] Solid056
  shape: bbox 5.588 x 6.511 x 7.325 mm, 28 faces (baked)
FEATURE [Part::Feature] Solid057
  shape: bbox 4.235 x 11.94 x 4.237 mm, 7 faces (baked)
FEATURE [Part::Feature] Solid058
  shape: bbox 11.94 x 4.155 x 4.16 mm, 7 faces (baked)
FEATURE [Part::Feature] Solid059
  shape: bbox 26.29 x 26.29 x 2.032 mm, 29 faces (baked)
FEATURE [Part::Compound2] Compound012  label="3055-E0W"
  Links = -> [Solid047,Solid048,Solid049,Solid050,Solid051,Solid052,Solid053,Solid054,Solid055,Solid056,Solid057,Solid058,Solid059]
  Placement = pos=(-1.5,-0.4,121.5) rot=(1,0,0;1.5708rad)
FEATURE [App::Part] Part011  label="Fiber"
  Group = -> [Solid039,Solid045,Solid040,Solid038,Solid042,Solid046,Solid041,Compound011,Solid043,Solid044,Compound010,Solid053,Solid052,Solid057,Solid058,Solid059,Solid055,Solid054,Solid056,Solid047,Solid048,Solid049,Solid050,Solid051,Compound012]
  Origin = -> Origin056
  Placement = pos=(127,1200,19.05) rot=(0,0,1;3.14159rad)
